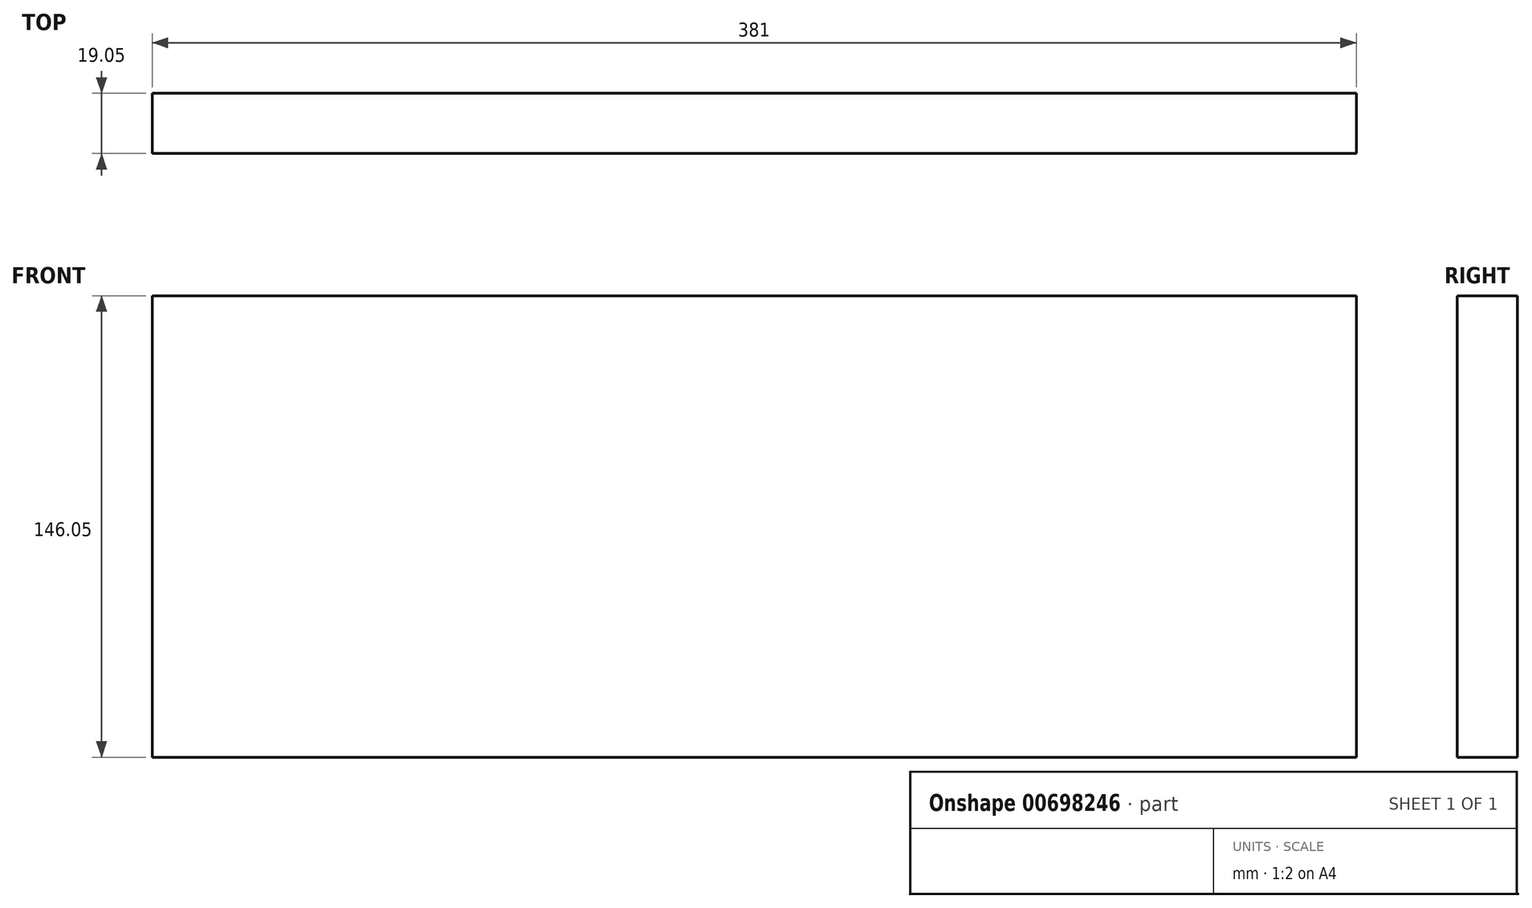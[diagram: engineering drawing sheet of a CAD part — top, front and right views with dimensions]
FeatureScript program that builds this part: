
annotation { "Feature Type Name" : "Feature", "Feature Type Description" : "" }
export const myFeature = defineFeature(function(context is Context, id is Id, definition is map)
    precondition{}
    {
        {
            var Q0;
            Q0=qCreatedBy(makeId("Front.planeOp"),FACE);
            var sketch = newSketch(context, id + "F0", { "sketchPlane" : qUnion([Q0])});
            skLineSegment(sketch, "E0.bottom", {"start": v(-196.28, -65.53) * mm, "end": v(184.72, -65.53) * mm});
            skLineSegment(sketch, "E0.top", {"start": v(-196.28, 80.52) * mm, "end": v(184.72, 80.52) * mm});
            skLineSegment(sketch, "E0.left", {"start": v(-196.28, -65.53) * mm, "end": v(-196.28, 80.52) * mm});
            skLineSegment(sketch, "E0.right", {"start": v(184.72, -65.53) * mm, "end": v(184.72, 80.52) * mm});
            skSolve(sketch);
        }
        {
            var Q0;
            Q0 = qSketchRegion(id + "F0", true);
            extrude(context, id + "F1", {"entities" : qUnion([Q0]), "depth" : 19.05 * mm, "offsetDistance" : 25.4 * mm});
        }
    });
